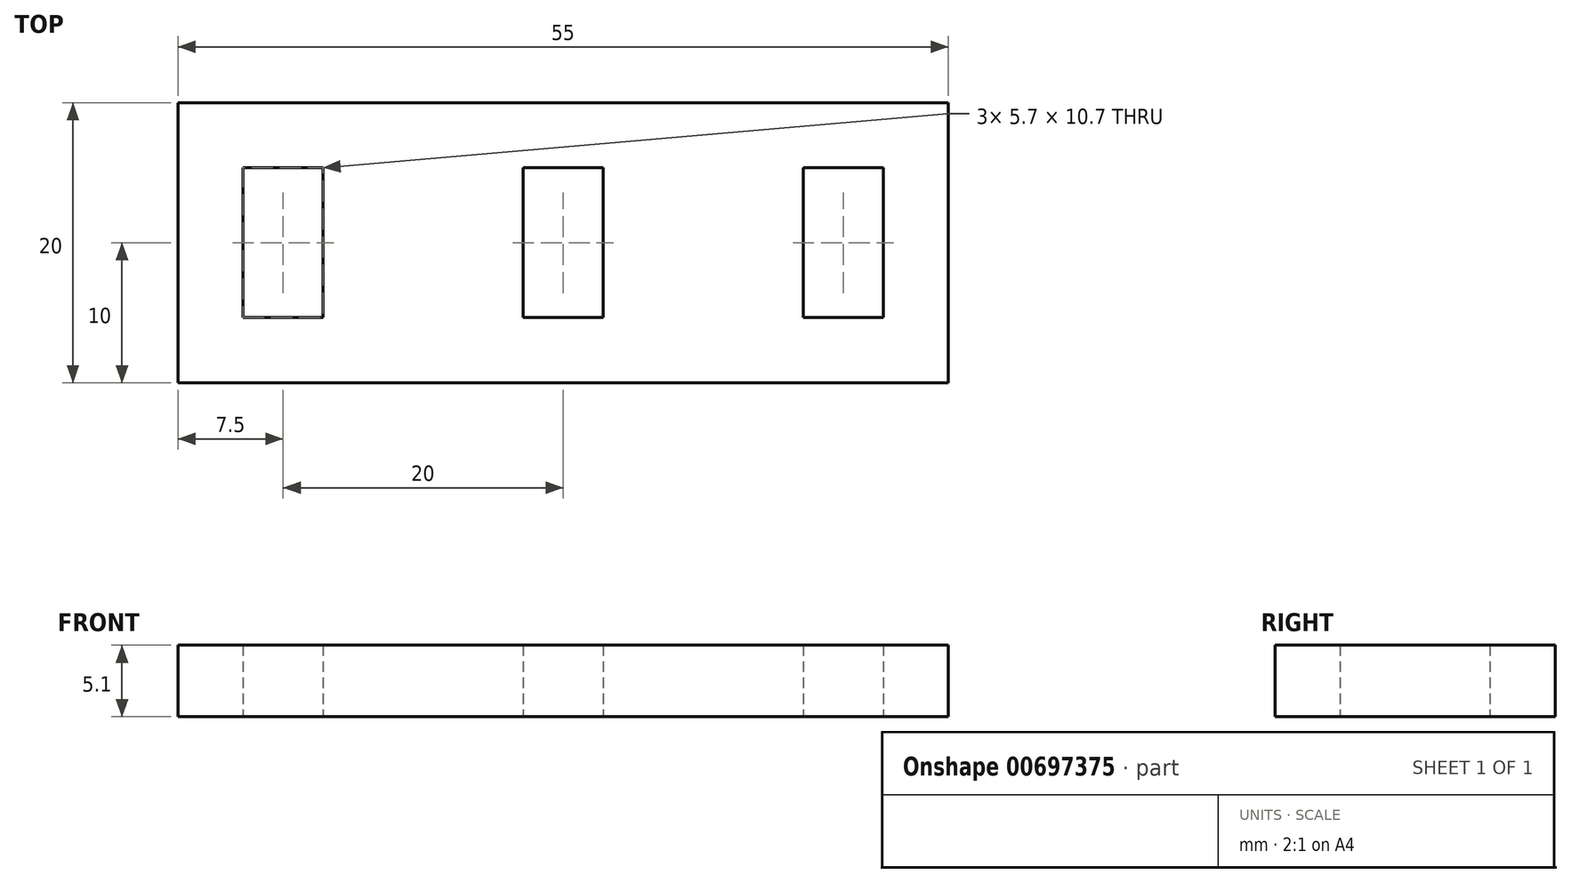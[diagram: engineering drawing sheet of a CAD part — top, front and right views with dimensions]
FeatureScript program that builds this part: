
annotation { "Feature Type Name" : "Feature", "Feature Type Description" : "" }
export const myFeature = defineFeature(function(context is Context, id is Id, definition is map)
    precondition{}
    {
        {
            var Q0;
            Q0=qCreatedBy(makeId("Top.planeOp"),FACE);
            var sketch = newSketch(context, id + "F0", { "sketchPlane" : qUnion([Q0])});
            skLineSegment(sketch, "E0.bottom", {"start": v(-22.5, 5) * mm, "end": v(22.5, 5) * mm});
            skLineSegment(sketch, "E0.top", {"start": v(-22.5, -5) * mm, "end": v(22.5, -5) * mm});
            skLineSegment(sketch, "E0.left", {"start": v(-22.5, 5) * mm, "end": v(-22.5, -5) * mm});
            skLineSegment(sketch, "E0.right", {"start": v(22.5, 5) * mm, "end": v(22.5, -5) * mm});
            skLineSegment(sketch, "E1", {"start": v(-17.5, 5) * mm, "end": v(-17.5, -5) * mm});
            skLineSegment(sketch, "E2.bottom", {"start": v(-2.5, 5) * mm, "end": v(2.5, 5) * mm});
            skLineSegment(sketch, "E2.top", {"start": v(-2.5, -5) * mm, "end": v(2.5, -5) * mm});
            skLineSegment(sketch, "E2.left", {"start": v(-2.5, 5) * mm, "end": v(-2.5, -5) * mm});
            skLineSegment(sketch, "E2.right", {"start": v(2.5, 5) * mm, "end": v(2.5, -5) * mm});
            skLineSegment(sketch, "E3.MirrorCS", {"start": v(17.5, 5) * mm, "end": v(17.5, -5) * mm});
            skLineSegment(sketch, "E4.bottom", {"start": v(-27.5, 10) * mm, "end": v(27.5, 10) * mm});
            skLineSegment(sketch, "E4.top", {"start": v(-27.5, -10) * mm, "end": v(27.5, -10) * mm});
            skLineSegment(sketch, "E4.left", {"start": v(-27.5, 10) * mm, "end": v(-27.5, -10) * mm});
            skLineSegment(sketch, "E4.right", {"start": v(27.5, 10) * mm, "end": v(27.5, -10) * mm});
            skLineSegment(sketch, "E5.bottom", {"start": v(-22.85, 5.35) * mm, "end": v(-17.15, 5.35) * mm});
            skLineSegment(sketch, "E5.top", {"start": v(-22.85, -5.35) * mm, "end": v(-17.15, -5.35) * mm});
            skLineSegment(sketch, "E5.left", {"start": v(-22.85, 5.35) * mm, "end": v(-22.85, -5.35) * mm});
            skLineSegment(sketch, "E5.right", {"start": v(-17.15, 5.35) * mm, "end": v(-17.15, -5.35) * mm});
            skLineSegment(sketch, "E6.MirrorCS", {"start": v(22.85, 5.35) * mm, "end": v(17.15, 5.35) * mm});
            skLineSegment(sketch, "E7.MirrorCS", {"start": v(22.85, 5.35) * mm, "end": v(22.85, -5.35) * mm});
            skLineSegment(sketch, "E8.MirrorCS", {"start": v(17.15, 5.35) * mm, "end": v(17.15, -5.35) * mm});
            skLineSegment(sketch, "E9.MirrorCS", {"start": v(22.85, -5.35) * mm, "end": v(17.15, -5.35) * mm});
            skLineSegment(sketch, "E10.bottom", {"start": v(-2.85, 5.35) * mm, "end": v(2.85, 5.35) * mm});
            skLineSegment(sketch, "E10.top", {"start": v(-2.85, -5.35) * mm, "end": v(2.85, -5.35) * mm});
            skLineSegment(sketch, "E10.left", {"start": v(-2.85, 5.35) * mm, "end": v(-2.85, -5.35) * mm});
            skLineSegment(sketch, "E10.right", {"start": v(2.85, 5.35) * mm, "end": v(2.85, -5.35) * mm});
            skSolve(sketch);
        }
        {
            var Q0;
            Q0=makeQuery(id+"F0.imprint","IMPRINT",FACE,{"disambiguationData":[TD([[makeQuery(id+"F0.imprint","IMPRINT",EDGE,{"derivedFrom":sQuery(id+"F0.wireOp",EDGE,"E4.bottom")}),-1.0]])]});
            var Q1;
            {var subQ0=sQuery(id+"F0.wireOp",EDGE,"E5.right");var subQ1=sQuery(id+"F0.wireOp",EDGE,"E0.bottom");var subQ2=makeQuery(id+"F0.imprint","INTERSECT",VERTEX,{"derivedFrom":[subQ1,subQ0]});Q1=makeQuery(id+"F0.imprint","IMPRINT",FACE,{"disambiguationData":[TD([[makeQuery(id+"F0.imprint","IMPRINT",EDGE,{"disambiguationData":[TD([[subQ2,-1.0]])],"derivedFrom":subQ1}),-1.0]])]});}
            var Q2;
            {var subQ0=sQuery(id+"F0.wireOp",EDGE,"E10.right");var subQ1=sQuery(id+"F0.wireOp",EDGE,"E0.bottom");var subQ2=makeQuery(id+"F0.imprint","INTERSECT",VERTEX,{"derivedFrom":[subQ1,subQ0]});Q2=makeQuery(id+"F0.imprint","IMPRINT",FACE,{"disambiguationData":[TD([[makeQuery(id+"F0.imprint","IMPRINT",EDGE,{"disambiguationData":[TD([[subQ2,-1.0]])],"derivedFrom":subQ1}),-1.0]])]});}
            extrude(context, id + "F1", {"entities" : qUnion([Q0, Q1, Q2]), "depth" : 5.1 * mm, "offsetDistance" : 25 * mm});
        }
    });
